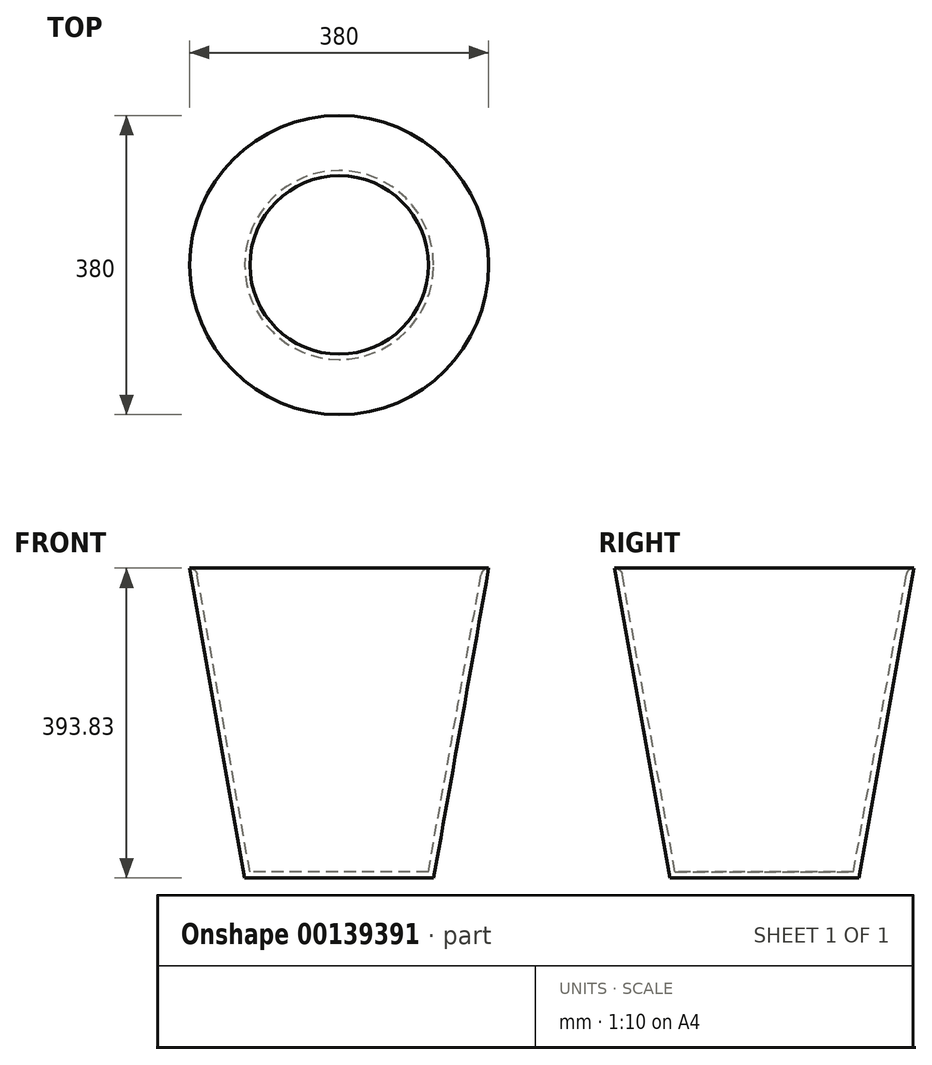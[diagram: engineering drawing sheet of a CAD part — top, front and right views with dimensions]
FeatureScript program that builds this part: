
annotation { "Feature Type Name" : "Feature", "Feature Type Description" : "" }
export const myFeature = defineFeature(function(context is Context, id is Id, definition is map)
    precondition{}
    {
        {
            var Q0;
            Q0=qCreatedBy(makeId("Front.planeOp"),FACE);
            var sketch = newSketch(context, id + "F0", { "sketchPlane" : qUnion([Q0])});
            skLineSegment(sketch, "E0", {"start": v(0, 0) * mm, "end": v(-120, 0) * mm});
            skLineSegment(sketch, "E1", {"start": v(-120, 0) * mm, "end": v(-190, 393.83) * mm});
            skLineSegment(sketch, "E2", {"start": v(-190, 393.83) * mm, "end": v(0, 393.83) * mm});
            skLineSegment(sketch, "E3", {"start": v(0, 393.83) * mm, "end": v(0, 0) * mm});
            skSolve(sketch);
        }
        {
            var Q0;
            Q0 = qSketchRegion(id + "F0", true);
            var Q1;
            Q1=sQuery(id+"F0.wireOp",EDGE,"E3");
            revolve(context, id + "F1", {"entities" : qUnion([Q0]), "axis" : qUnion([Q1]), "revolveType" : RevolveType.FULL});
        }
        {
            var Q0;
            Q0=makeQuery(id+"F1.opRevolve","SWEPT_FACE",FACE,{"disambiguationData":[OSD([sQuery(id+"F0.wireOp",EDGE,"E2")])]});
            shell(context, id + "F2", {"entities" : qUnion([Q0]), "thickness" : 8 * mm});
        }
        {
            var Q0;
            Q0=makeQuery(id+"F2.opShell","OFFSET_EDGE",EDGE,{"disambiguationData":[OSD([sQuery(id+"F0.wireOp",EDGE,"E1"),sQuery(id+"F0.wireOp",EDGE,"E2")])]});
            fillet(context, id + "F3", {"entities" : qUnion([Q0]), "radius" : 10 * mm, "tangentPropagation" : true, "allowEdgeOverflow" : false});
        }
    });
